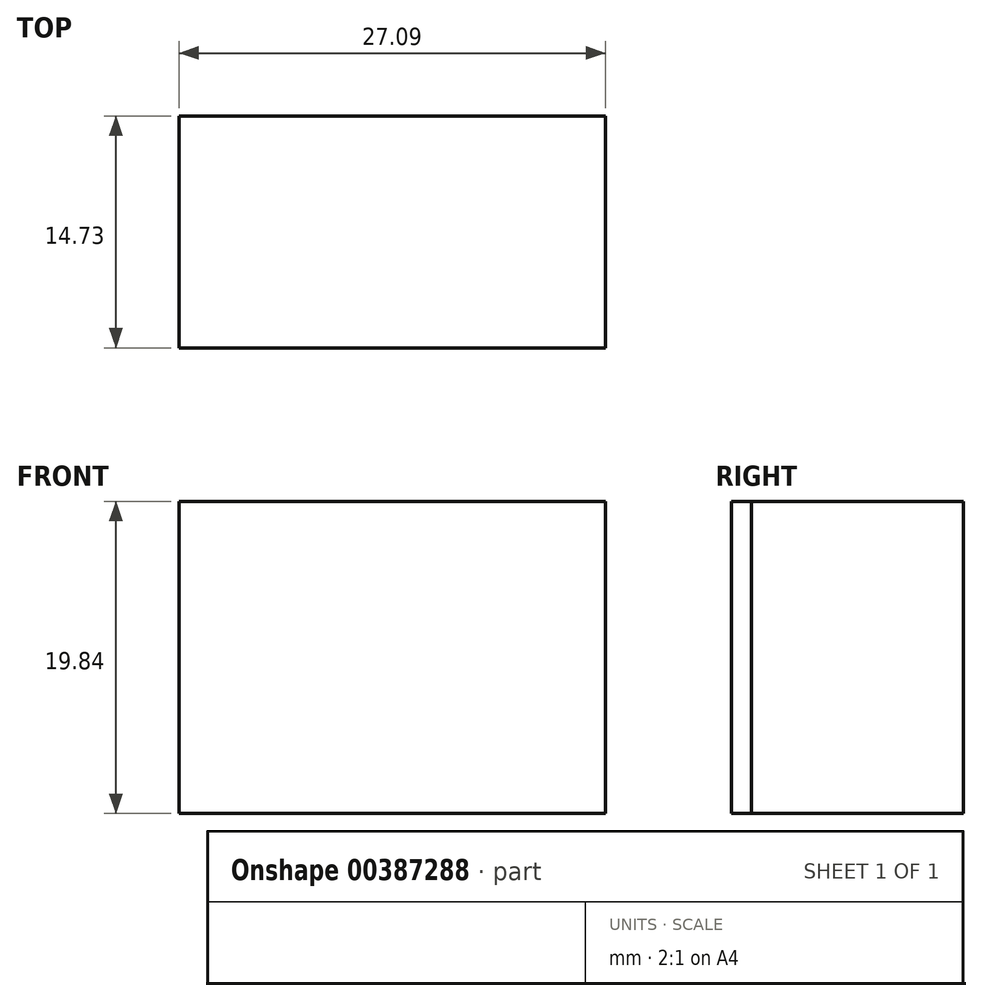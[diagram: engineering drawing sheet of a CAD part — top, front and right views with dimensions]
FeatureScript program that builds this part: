
annotation { "Feature Type Name" : "Feature", "Feature Type Description" : "" }
export const myFeature = defineFeature(function(context is Context, id is Id, definition is map)
    precondition{}
    {
        {
            var Q0;
            Q0=qCreatedBy(makeId("Front.planeOp"),FACE);
            var sketch = newSketch(context, id + "F0", { "sketchPlane" : qUnion([Q0])});
            skLineSegment(sketch, "E0", {"start": v(-31.43, 0) * mm, "end": v(-31.43, 19.84) * mm});
            skLineSegment(sketch, "E1", {"start": v(-4.34, 19.84) * mm, "end": v(-4.34, 0) * mm});
            skLineSegment(sketch, "E2", {"start": v(-4.34, 0) * mm, "end": v(-31.43, 0) * mm});
            skLineSegment(sketch, "E3", {"start": v(-31.43, 19.84) * mm, "end": v(-4.34, 19.84) * mm});
            skSolve(sketch);
        }
        {
            var Q0;
            Q0=sQuery(id+"F0.wireOp",EDGE,"E1");
            extrude(context, id + "F1", {"bodyType" : ToolBodyType.SURFACE, "surfaceEntities" : qUnion([Q0]), "depth" : 13.46 * mm});
        }
        {
            var Q0;
            Q0=sQuery(id+"F0.wireOp",EDGE,"E0");
            var Q1;
            Q1=sQuery(id+"F0.wireOp",EDGE,"E3");
            var Q2;
            Q2=sQuery(id+"F0.wireOp",EDGE,"E1");
            var Q3;
            Q3=sQuery(id+"F0.wireOp",EDGE,"E2");
            extrude(context, id + "F2", {"bodyType" : ToolBodyType.SURFACE, "surfaceEntities" : qUnion([Q0, Q1, Q2, Q3]), "depth" : 14.73 * mm});
        }
    });
